# Revit family: IS_Oleas_R0123_BIM_NN
name_source: partatom
category: Plumbing Fixtures
revit_build: Autodesk Revit 2017 (Build: 20160225_1515(x64)
units: mm (PartAtom-declared; Revit-internal decimal feet)

## family parameters
Cut with Voids When Loaded = No
Host = Face
OmniClass Number = 23.45.05.21.11.11
OmniClass Title = Water Operated Water Closets
Part Type = Normal
Room Calculation Point = No
Round Connector Dimension = Use Diameter
Shared = Yes

## types (4) — shared parameters
Accessories = www.idealspec.co.uk
AreaUnits = millimeters
Assembly Code = C1030200
AssetType = Fixed
BREEAMApproved = No
Brand = Ideal Standard
ConnectionType = Plumbing
DurationUnit = year
ECA = No
Help = www.idealspec.co.uk/contact-us.html
IfcExportAs = IfcSanitaryTerminalType
IfcExportType = CISTERN
InstallationInstructions = www.idealspec.co.uk/resources.html
LinearUnits = millimeters
ManufacturerURL = www.idealspec.co.uk
NBSDescription = WC cistern fittings
NBSReference = 45-30-70/387
NominalDepth = 7 mm  [stored 0.0229659 ft]
NominalHeight = 150 mm
NominalLength = 7 mm  [stored 0.0229659 ft]
NominalWidth = 230 mm
Shape = Sculptured
Size = 230 x 150 x 7 mm
Space = Internal
ToiletPanType = WashDown
ToiletType = Other
URL = www.idealspec.co.uk
Uniclass2 = Pr_40_20_93_89
Uniclass2015Code = Pr_40_20_93_89
Uniclass2015Description = WC cisterns
Uniclass2015Version = 1
Version = 1
VolumeUnits = Litres
WRAS = No
WarrantyDescription = Manufacturers Warranty
WarrantyDurationParts = 0
WarrantyDurationUnit = year
WaterEfficientProduct = No
zero-valued in all types: CWFU, Cost, Default Elevation, HWFU, SpilloverLevel, WFU

## per-type parameters (varying)
| type | BIMObjectName | BarCode | Description | Finish | Flush Plate Material | Model | ModelNumber | ModelReference | Name | ProductInformation |
| R0123AA - OLEAS M3 CHROME - IS | IS_Ideal Standard_WC cistern fittings_Oleas_R0123AA | 3391500580398 | New 3 Soft Square button plate, CP DF - mechanicals IS | Chrome | Chrome-Polished | R0123AA | R0123AA | New 3 Soft Square button plate, CP DF - mechanicals IS | WC cistern fittings_Oleas_R0123AA_Ideal Standard | www.idealspec.co.uk/assets/datasheet/R0123AA |
| R0123AC - OLEAS M3 WHITE - IS | IS_Ideal Standard_WC cistern fittings_Oleas_R0123AC | 3391500580404 | New 3 Soft Square button plate, WH DF - mechanical IS | White | Plactic-White | R0123AC | R0123AC | New 3 Soft Square button plate, WH DF - mechanical IS | WC cistern fittings_Oleas_R0123AC_Ideal Standard | www.idealspec.co.uk/assets/datasheet/R0123AC |
| R0123JG - OLEAS M3 MATT CHROME - IS | IS_Ideal Standard_WC cistern fittings_Oleas_R0123JG | 3391500580411 | New 3 Soft Square button plate, Matt DF - mechanical IS | Matt Chrome | Chrome-Matt | R0123JG | R0123JG | New 3 Soft Square button plate, Matt DF - mechanical IS | WC cistern fittings_Oleas_R0123JG_Ideal Standard | www.idealspec.co.uk/assets/datasheet/R0123JG |
| R0123A6 - OLEAS M3 BLACK - IS | IS_Ideal Standard_WC cistern fittings_Oleas_R0123A6 | 3391500580381 | New 3 Soft Square button plate - mechanical IS | Chrome | Plastic-Black | R0123A6 | R0123A6 | New 3 Soft Square button plate - mechanical IS | WC cistern fittings_Oleas_R0123A6_Ideal Standard | www.idealspec.co.uk/assets/datasheet/R0123A6 |

note: [stored X ft] marks values corroborated as IEEE doubles in the binary element streams (Revit-internal decimal feet)

## geometry (parser evidence)
native form markers: Sweep x3
no freeform markers — native parametric forms only
